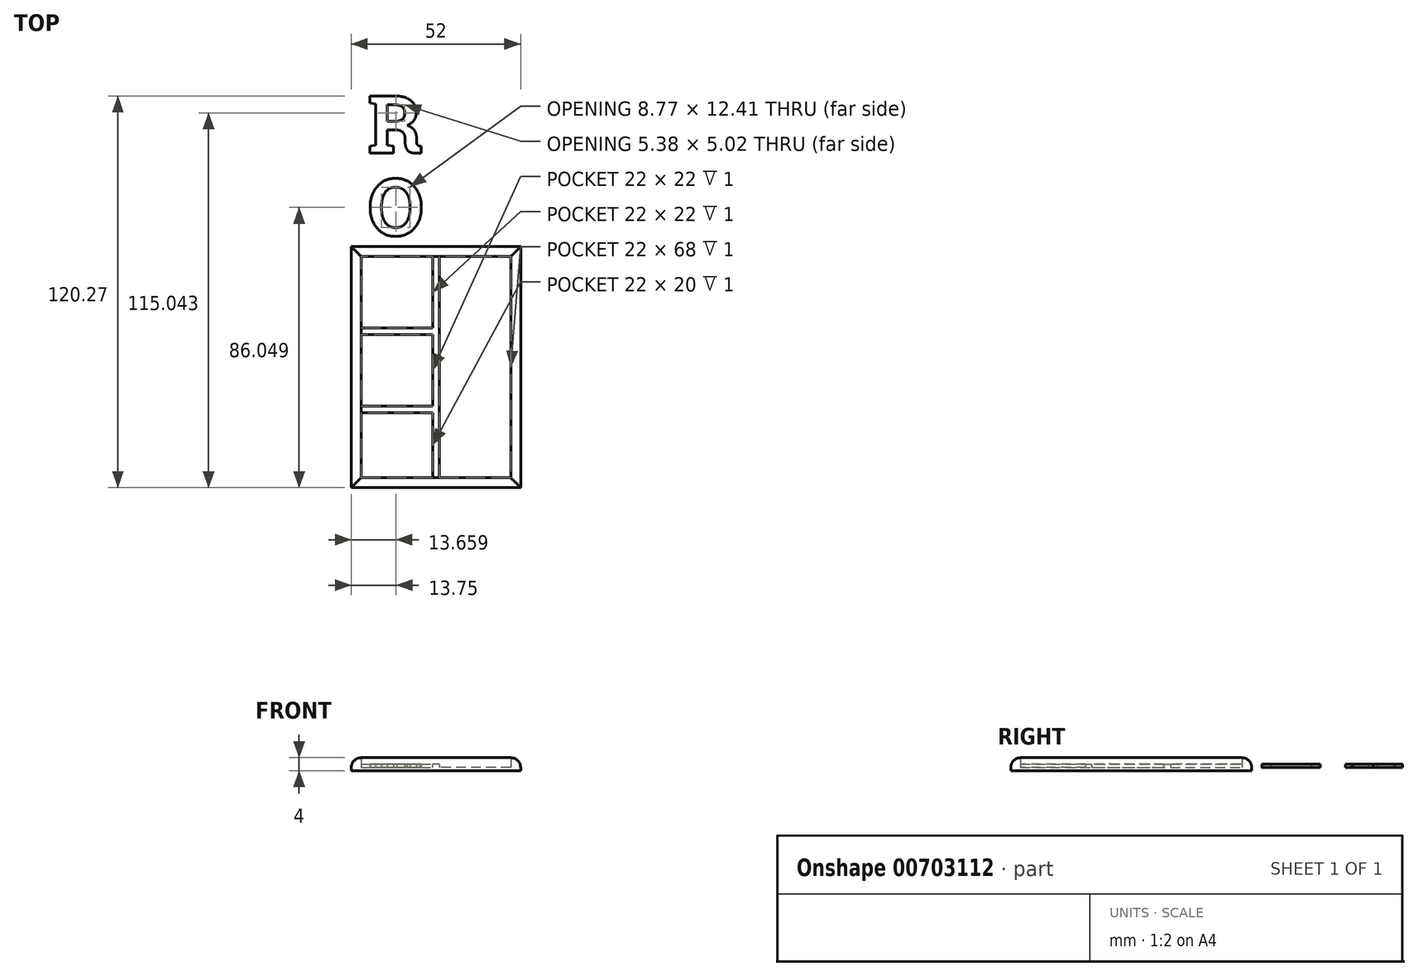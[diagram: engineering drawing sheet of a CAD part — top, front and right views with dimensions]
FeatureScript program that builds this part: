
annotation { "Feature Type Name" : "Feature", "Feature Type Description" : "" }
export const myFeature = defineFeature(function(context is Context, id is Id, definition is map)
    precondition{}
    {
        {
            var Q0;
            Q0=qCreatedBy(makeId("Top.planeOp"),FACE);
            var sketch = newSketch(context, id + "F0", { "sketchPlane" : qUnion([Q0])});
            skLineSegment(sketch, "E0.bottom", {"start": v(-26, 1.1) * mm, "end": v(26, 1.1) * mm});
            skLineSegment(sketch, "E0.top", {"start": v(-26, -72.9) * mm, "end": v(26, -72.9) * mm});
            skLineSegment(sketch, "E0.left", {"start": v(-26, 1.1) * mm, "end": v(-26, -72.9) * mm});
            skLineSegment(sketch, "E0.right", {"start": v(26, 1.1) * mm, "end": v(26, -72.9) * mm});
            skLineSegment(sketch, "E1.bottom", {"start": v(23, -69.9) * mm, "end": v(-23, -69.9) * mm});
            skLineSegment(sketch, "E1.top", {"start": v(23, -1.9) * mm, "end": v(-23, -1.9) * mm});
            skLineSegment(sketch, "E1.left", {"start": v(23, -69.9) * mm, "end": v(23, -1.9) * mm});
            skLineSegment(sketch, "E1.right", {"start": v(-23, -69.9) * mm, "end": v(-23, -1.9) * mm});
            skLineSegment(sketch, "E2", {"start": v(-1, -1.9) * mm, "end": v(-1, -69.9) * mm});
            skLineSegment(sketch, "E3", {"start": v(1, -69.9) * mm, "end": v(1, -1.9) * mm});
            skLineSegment(sketch, "E4.direction1", {"start": v(1, -69.9) * mm, "end": v(23, -69.9) * mm, "construction": true});
            skSolve(sketch);
        }
        {
            var Q0;
            Q0=makeQuery(id+"F0.imprint","IMPRINT",FACE,{"disambiguationData":[TD([[makeQuery(id+"F0.imprint","IMPRINT",EDGE,{"derivedFrom":sQuery(id+"F0.wireOp",EDGE,"E0.bottom")}),-1.0]])]});
            var Q1;
            Q1=sQuery(id+"F0.wireOp",EDGE,"E1.top");
            var Q2;
            Q2=sQuery(id+"Fu5JrzOHV6ZgCpF_0.wireOp",EDGE,"1024a238-9103-462a-9477-26902ec0aa7303");
            var Q3;
            Q3=sQuery(id+"F0.wireOp",EDGE,"E0.bottom");
            var Q4;
            Q4=sQuery(id+"F0.wireOp",EDGE,"E1.right");
            var Q5;
            Q5=sQuery(id+"F0.wireOp",EDGE,"E0.left");
            var Q6;
            Q6=sQuery(id+"F0.wireOp",EDGE,"E0.top");
            var Q7;
            Q7=sQuery(id+"F0.wireOp",EDGE,"E1.bottom");
            var Q8;
            Q8=sQuery(id+"Fu5JrzOHV6ZgCpF_0.wireOp",EDGE,"1024a238-9103-462a-9477-26902ec0aa7301");
            var Q9;
            Q9=sQuery(id+"F0.wireOp",EDGE,"E1.left");
            var Q10;
            Q10=sQuery(id+"F0.wireOp",EDGE,"E0.right");
            extrude(context, id + "F1", {"entities" : qUnion([Q0]), "surfaceEntities" : qUnion([Q1, Q2, Q3, Q4, Q5, Q6, Q7, Q8, Q9, Q10]), "depth" : 3 * mm, "offsetDistance" : 25 * mm});
        }
        {
            var Q0;
            {var subQ0=sQuery(id+"F0.wireOp",EDGE,"E2");Q0=makeQuery(id+"F0.imprint","IMPRINT",FACE,{"disambiguationData":[TD([[makeQuery(id+"F0.imprint","IMPRINT",EDGE,{"derivedFrom":subQ0}),1.0]])]});}
            var Q1;
            {var subQ0=sQuery(id+"F0.wireOp",EDGE,"e9ec2e05-978c-41d5-a06a-ce314fcd9169.1.0.0");Q1=makeQuery(id+"F0.imprint","IMPRINT",FACE,{"disambiguationData":[TD([[makeQuery(id+"F0.imprint","IMPRINT",EDGE,{"derivedFrom":subQ0}),1.0]])]});}
            var Q2;
            {var subQ0=sQuery(id+"F0.wireOp",EDGE,"e9ec2e05-978c-41d5-a06a-ce314fcd9169.2.0.0");Q2=makeQuery(id+"F0.imprint","IMPRINT",FACE,{"disambiguationData":[TD([[makeQuery(id+"F0.imprint","IMPRINT",EDGE,{"derivedFrom":subQ0}),1.0]])]});}
            var Q3;
            Q3=sQuery(id+"F0.wireOp",EDGE,"E2");
            var Q4;
            Q4=sQuery(id+"F0.wireOp",EDGE,"E3");
            extrude(context, id + "F2", {"entities" : qUnion([Q0, Q1, Q2]), "operationType" : NewBodyOperationType.ADD, "surfaceEntities" : qUnion([Q3, Q4]), "depth" : 1 * mm, "offsetDistance" : 25 * mm});
        }
        {
            var Q0;
            Q0=makeQuery(id+"F1.opExtrude","CAP_EDGE",EDGE,{"disambiguationData":[OSD([sQuery(id+"F0.wireOp",EDGE,"E0.right")])],"isStart":false});
            var Q1;
            Q1=makeQuery(id+"F1.opExtrude","CAP_EDGE",EDGE,{"disambiguationData":[OSD([sQuery(id+"F0.wireOp",EDGE,"E0.top")])],"isStart":false});
            var Q2;
            Q2=makeQuery(id+"F1.opExtrude","CAP_EDGE",EDGE,{"disambiguationData":[OSD([sQuery(id+"F0.wireOp",EDGE,"E0.left")])],"isStart":false});
            var Q3;
            Q3=makeQuery(id+"F1.opExtrude","CAP_EDGE",EDGE,{"disambiguationData":[OSD([sQuery(id+"F0.wireOp",EDGE,"E0.bottom")])],"isStart":false});
            fillet(context, id + "F3", {"entities" : qUnion([Q0, Q1, Q2, Q3]), "radius" : 3 * mm, "tangentPropagation" : true, "allowEdgeOverflow" : false});
        }
        {
            var Q0;
            Q0=qCreatedBy(makeId("Top.planeOp"),FACE);
            var sketch = newSketch(context, id + "F4", { "sketchPlane" : qUnion([Q0])});
            skLineSegment(sketch, "E5.bottom", {"start": v(-26, -72.9) * mm, "end": v(26, -72.9) * mm});
            skLineSegment(sketch, "E5.top", {"start": v(-26, 1.1) * mm, "end": v(26, 1.1) * mm});
            skLineSegment(sketch, "E5.left", {"start": v(-26, -72.9) * mm, "end": v(-26, 1.1) * mm});
            skLineSegment(sketch, "E5.right", {"start": v(26, -72.9) * mm, "end": v(26, 1.1) * mm});
            skSolve(sketch);
        }
        {
            var Q0;
            Q0=qSketchRegion(id+"F4",true);
            extrude(context, id + "F5", {"entities" : qUnion([Q0]), "operationType" : NewBodyOperationType.ADD, "oppositeDirection" : true, "depth" : 1 * mm, "offsetDistance" : 25 * mm});
        }
        {
            var Q0;
            Q0=qCreatedBy(makeId("Top.planeOp"),FACE);
            var sketch = newSketch(context, id + "F6", { "sketchPlane" : qUnion([Q0])});
            skText(sketch, "E6", { "text": "R", "fontName": "RobotoSlab-Bold.ttf"});
            const initialGuessF6  = {"E6": [-0.021, 0.02983, 1, 0, 0.01777]};
            skSetInitialGuess(sketch, initialGuessF6);
            skSolve(sketch);
        }
        {
            var Q0;
            Q0=qCreatedBy(makeId("Top.planeOp"),FACE);
            var sketch = newSketch(context, id + "F7", { "sketchPlane" : qUnion([Q0])});
            skText(sketch, "E7", { "text": "O", "fontName": "RobotoSlab-Bold.ttf"});
            const initialGuessF7  = {"E7": [-0.021, 0.0045, 1, 0, 0.01755], "E7": [-0.021, 0.0045, 1, 0, 0.01755]};
            skSetInitialGuess(sketch, initialGuessF7);
            skSolve(sketch);
        }
        {
            var Q0;
            Q0=qSketchRegion(id+"F6",true);
            extrude(context, id + "F8", {"entities" : qUnion([Q0]), "operationType" : NewBodyOperationType.ADD, "depth" : 1 * mm, "offsetDistance" : 25 * mm});
        }
        {
            var Q0;
            Q0=qSketchRegion(id+"F7",true);
            extrude(context, id + "F9", {"entities" : qUnion([Q0]), "operationType" : NewBodyOperationType.ADD, "depth" : 1 * mm, "offsetDistance" : 25 * mm});
        }
        {
            var Q0;
            Q0=qCreatedBy(makeId("Top.planeOp"),FACE);
            var sketch = newSketch(context, id + "F10", { "sketchPlane" : qUnion([Q0])});
            skText(sketch, "E8", { "text": "L", "fontName": "RobotoSlab-Bold.ttf"});
            const initialGuessF10  = {"E8": [-0.02022, -0.01872, 1, 0, 0.019]};
            skSetInitialGuess(sketch, initialGuessF10);
            skSolve(sketch);
        }
        {
            var Q0;
            Q0=qCreatedBy(makeId("Top.planeOp"),FACE);
            var sketch = newSketch(context, id + "F11", { "sketchPlane" : qUnion([Q0])});
            skText(sketch, "E9", { "text": "L", "fontName": "RobotoSlab-Bold.ttf"});
            const initialGuessF11  = {"E9": [-0.02022, -0.0455, 1, 0, 0.019]};
            skSetInitialGuess(sketch, initialGuessF11);
            skSolve(sketch);
        }
        {
            var Q0;
            Q0=qCreatedBy(makeId("Top.planeOp"),FACE);
            var sketch = newSketch(context, id + "F12", { "sketchPlane" : qUnion([Q0])});
            skText(sketch, "E10", { "text": "K", "fontName": "RobotoSlab-Bold.ttf"});
            const initialGuessF12  = {"E10": [0.027, 0.03057, 1, 0, 0.01703]};
            skSetInitialGuess(sketch, initialGuessF12);
            skSolve(sketch);
        }
        {
            var Q0;
            Q0=qCreatedBy(makeId("Top.planeOp"),FACE);
            var sketch = newSketch(context, id + "F13", { "sketchPlane" : qUnion([Q0])});
            skText(sketch, "E11", { "text": "E", "fontName": "RobotoSlab-Bold.ttf"});
            const initialGuessF13  = {"E11": [0.0274, 0.00557, 1, 0, 0.019]};
            skSetInitialGuess(sketch, initialGuessF13);
            skSolve(sketch);
        }
        {
            var Q0;
            Q0=qCreatedBy(makeId("Top.planeOp"),FACE);
            var sketch = newSketch(context, id + "F14", { "sketchPlane" : qUnion([Q0])});
            skText(sketch, "E12", { "text": "E", "fontName": "RobotoSlab-Bold.ttf"});
            const initialGuessF14  = {"E12": [0.0274, -0.01943, 1, 0, 0.019]};
            skSetInitialGuess(sketch, initialGuessF14);
            skSolve(sketch);
        }
        {
            var Q0;
            Q0=qCreatedBy(makeId("Top.planeOp"),FACE);
            var sketch = newSketch(context, id + "F15", { "sketchPlane" : qUnion([Q0])});
            skText(sketch, "E13", { "text": "P", "fontName": "RobotoSlab-Bold.ttf"});
            const initialGuessF15  = {"E13": [0.027, -0.0442, 1, 0, 0.01878]};
            skSetInitialGuess(sketch, initialGuessF15);
            skSolve(sketch);
        }
        {
            var Q0;
            Q0=qCreatedBy(makeId("Top.planeOp"),FACE);
            var sketch = newSketch(context, id + "F16", { "sketchPlane" : qUnion([Q0])});
            skLineSegment(sketch, "E14.bottom", {"start": v(-24, -23.9) * mm, "end": v(0, -23.9) * mm});
            skLineSegment(sketch, "E14.top", {"start": v(-24, -25.9) * mm, "end": v(0, -25.9) * mm});
            skLineSegment(sketch, "E14.left", {"start": v(-24, -23.9) * mm, "end": v(-24, -25.9) * mm});
            skLineSegment(sketch, "E14.right", {"start": v(0, -23.9) * mm, "end": v(0, -25.9) * mm});
            skLineSegment(sketch, "E15.bottom", {"start": v(-24, -47.9) * mm, "end": v(0, -47.9) * mm});
            skLineSegment(sketch, "E15.top", {"start": v(-24, -49.9) * mm, "end": v(0, -49.9) * mm});
            skLineSegment(sketch, "E15.left", {"start": v(-24, -47.9) * mm, "end": v(-24, -49.9) * mm});
            skLineSegment(sketch, "E15.right", {"start": v(0, -47.9) * mm, "end": v(0, -49.9) * mm});
            skSolve(sketch);
        }
        {
            var Q0;
            Q0 = qSketchRegion(id + "F16", true);
            extrude(context, id + "F17", {"entities" : qUnion([Q0]), "operationType" : NewBodyOperationType.ADD, "depth" : 1 * mm, "offsetDistance" : 25 * mm});
        }
    });
